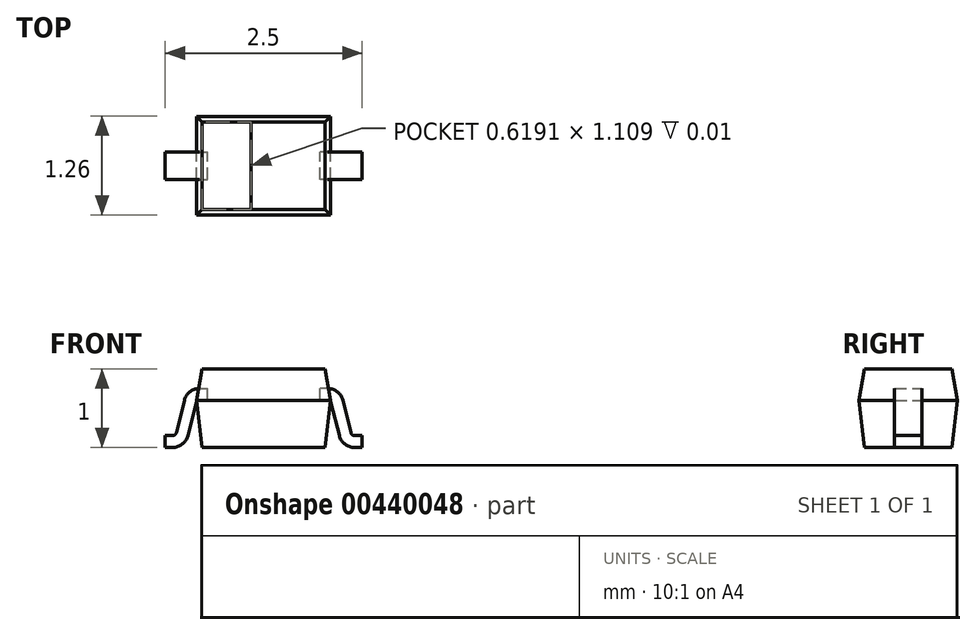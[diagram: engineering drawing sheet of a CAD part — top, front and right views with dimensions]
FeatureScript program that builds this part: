
annotation { "Feature Type Name" : "Feature", "Feature Type Description" : "" }
export const myFeature = defineFeature(function(context is Context, id is Id, definition is map)
    precondition{}
    {
        {
            var Q0;
            Q0=qCreatedBy(makeId("Front.planeOp"),FACE);
            var sketch = newSketch(context, id + "F0", { "sketchPlane" : qUnion([Q0])});
            skLineSegment(sketch, "E0", {"start": v(-0.85, 0) * mm, "end": v(0.85, 0) * mm});
            skLineSegment(sketch, "E1", {"start": v(0.85, 0) * mm, "end": v(0.78, 0.4) * mm});
            skLineSegment(sketch, "E2", {"start": v(0.78, 0.4) * mm, "end": v(-0.78, 0.4) * mm});
            skLineSegment(sketch, "E3", {"start": v(-0.78, 0.4) * mm, "end": v(-0.85, 0) * mm});
            skLineSegment(sketch, "E4", {"start": v(-0.85, 0) * mm, "end": v(-0.78, -0.6) * mm});
            skLineSegment(sketch, "E5", {"start": v(-0.78, -0.6) * mm, "end": v(0.78, -0.6) * mm});
            skLineSegment(sketch, "E6", {"start": v(0.78, -0.6) * mm, "end": v(0.85, 0) * mm});
            skLineSegment(sketch, "E7", {"start": v(0, 0.4) * mm, "end": v(0, -0.6) * mm});
            skSolve(sketch);
        }
        {
            var Q0;
            Q0 = qSketchRegion(id + "F0", true);
            extrude(context, id + "F1", {"entities" : qUnion([Q0]), "endBound" : BoundingType.SYMMETRIC, "depth" : 1.25 * mm});
        }
        {
            var Q0;
            Q0=qCreatedBy(makeId("Right.planeOp"),FACE);
            var sketch = newSketch(context, id + "F2", { "sketchPlane" : qUnion([Q0])});
            skLineSegment(sketch, "E8.0.0", {"start": v(0.62, -0.6) * mm, "end": v(0.62, 0) * mm});
            skLineSegment(sketch, "E8.0.1", {"start": v(0.62, 0) * mm, "end": v(-0.62, 0) * mm});
            skLineSegment(sketch, "E8.0.2", {"start": v(-0.62, 0) * mm, "end": v(-0.62, -0.6) * mm});
            skLineSegment(sketch, "E9.0.0", {"start": v(0.62, 0) * mm, "end": v(0.62, 0.4) * mm});
            skLineSegment(sketch, "E9.0.1", {"start": v(0.62, 0.4) * mm, "end": v(-0.62, 0.4) * mm});
            skLineSegment(sketch, "E9.0.2", {"start": v(-0.62, 0.4) * mm, "end": v(-0.62, 0) * mm});
            skLineSegment(sketch, "E9.0.3", {"start": v(-0.62, 0) * mm, "end": v(0.62, 0) * mm});
            skLineSegment(sketch, "E10", {"start": v(-0.63, 0) * mm, "end": v(-0.55, 0.4) * mm});
            skLineSegment(sketch, "E11", {"start": v(0.62, 0) * mm, "end": v(0.55, 0.4) * mm});
            skLineSegment(sketch, "E12", {"start": v(0.55, 0.4) * mm, "end": v(-0.55, 0.4) * mm});
            skLineSegment(sketch, "E13", {"start": v(-0.62, 0) * mm, "end": v(-0.55, -0.6) * mm});
            skLineSegment(sketch, "E14", {"start": v(0.62, 0) * mm, "end": v(0.55, -0.6) * mm});
            skLineSegment(sketch, "E15", {"start": v(0.55, -0.6) * mm, "end": v(-0.55, -0.6) * mm});
            skLineSegment(sketch, "E16", {"start": v(0, -0.6) * mm, "end": v(0, 0.4) * mm});
            skLineSegment(sketch, "E17.0", {"start": v(-0.62, -0.6) * mm, "end": v(0.62, -0.6) * mm});
            skLineSegment(sketch, "E18", {"start": v(-0.62, -0.6) * mm, "end": v(-0.55, -0.6) * mm});
            skSolve(sketch);
        }
        {
            var Q0;
            {var subQ0=sQuery(id+"F2.wireOp",EDGE,"E9.0.2");Q0=makeQuery(id+"F2.imprint","IMPRINT",FACE,{"disambiguationData":[TD([[makeQuery(id+"F2.imprint","IMPRINT",EDGE,{"derivedFrom":subQ0}),1.0]])]});}
            var Q1;
            Q1=makeQuery(id+"F2.imprint","IMPRINT",FACE,{"disambiguationData":[TD([[makeQuery(id+"F2.imprint","IMPRINT",EDGE,{"derivedFrom":sQuery(id+"F2.wireOp",EDGE,"E13")}),-1.0]])]});
            var Q2;
            {var subQ0=sQuery(id+"F2.wireOp",EDGE,"E8.0.0");Q2=makeQuery(id+"F2.imprint","IMPRINT",FACE,{"disambiguationData":[TD([[makeQuery(id+"F2.imprint","IMPRINT",EDGE,{"derivedFrom":subQ0}),1.0]])]});}
            var Q3;
            {var subQ0=sQuery(id+"F2.wireOp",EDGE,"E9.0.0");Q3=makeQuery(id+"F2.imprint","IMPRINT",FACE,{"disambiguationData":[TD([[makeQuery(id+"F2.imprint","IMPRINT",EDGE,{"derivedFrom":subQ0}),1.0]])]});}
            extrude(context, id + "F3", {"entities" : qUnion([Q0, Q1, Q2, Q3]), "operationType" : NewBodyOperationType.REMOVE, "endBound" : BoundingType.THROUGH_ALL, "oppositeDirection" : true, "depth" : 25 * mm, "hasSecondDirection" : true, "secondDirectionBound" : SecondDirectionBoundingType.THROUGH_ALL, "secondDirectionOppositeDirection" : false, "secondDirectionDepth" : 25 * mm});
        }
        {
            var Q0;
            Q0=qCreatedBy(makeId("Front.planeOp"),FACE);
            var sketch = newSketch(context, id + "F4", { "sketchPlane" : qUnion([Q0])});
            skLineSegment(sketch, "E19.0", {"start": v(-0.78, 0.4) * mm, "end": v(0.78, 0.4) * mm});
            skLineSegment(sketch, "E20.0", {"start": v(-0.78, -0.6) * mm, "end": v(0.78, -0.6) * mm});
            skLineSegment(sketch, "E21", {"start": v(0, 0.4) * mm, "end": v(0, -0.6) * mm});
            skLineSegment(sketch, "E22", {"start": v(1.25, -0.6) * mm, "end": v(-1.25, -0.6) * mm, "construction": true});
            skPoint(sketch, "E23.0", {"position": v(0.85, 0) * mm});
            skLineSegment(sketch, "E24", {"start": v(1.25, -0.6) * mm, "end": v(1.16, -0.6) * mm});
            skLineSegment(sketch, "E25", {"start": v(0.96, -0.45) * mm, "end": v(0.86, -0.04) * mm});
            skLineSegment(sketch, "E26", {"start": v(-1.25, -0.6) * mm, "end": v(-1.16, -0.6) * mm});
            skPoint(sketch, "E27.visualSharp", {"position": v(1, -0.6) * mm});
            skArc(sketch, "E27.filletArc", {"start": v(0.96, -0.45) * mm, "mid": v(1.03, -0.56) * mm, "end": v(1.16, -0.6) * mm});
            skLineSegment(sketch, "E28", {"start": v(0.81, 0) * mm, "end": v(0.71, 0) * mm});
            skArc(sketch, "E29.filletArc", {"start": v(0.86, -0.04) * mm, "mid": v(0.84, -0.01) * mm, "end": v(0.81, 0) * mm});
            skLineSegment(sketch, "E30.0", {"start": v(0.81, 0.15) * mm, "end": v(0.71, 0.15) * mm});
            skLineSegment(sketch, "E30.1", {"start": v(1.25, -0.45) * mm, "end": v(1.16, -0.45) * mm});
            skArc(sketch, "E30.2", {"start": v(1.1, -0.41) * mm, "mid": v(1.13, -0.44) * mm, "end": v(1.16, -0.45) * mm});
            skLineSegment(sketch, "E30.3", {"start": v(1.1, -0.41) * mm, "end": v(1, 0) * mm});
            skArc(sketch, "E30.4", {"start": v(1, 0) * mm, "mid": v(0.93, 0.1) * mm, "end": v(0.81, 0.15) * mm});
            skLineSegment(sketch, "E31", {"start": v(1.25, -0.6) * mm, "end": v(1.25, -0.45) * mm});
            skLineSegment(sketch, "E32", {"start": v(0.71, 0) * mm, "end": v(0.71, 0.15) * mm});
            skArc(sketch, "E33.MirrorCS", {"start": v(-0.86, -0.04) * mm, "mid": v(-0.84, -0.01) * mm, "end": v(-0.81, 0) * mm});
            skPoint(sketch, "E34.MirrorP", {"position": v(-0.85, 0) * mm});
            skLineSegment(sketch, "E35.MirrorCS", {"start": v(0.78, -0.6) * mm, "end": v(-0.78, -0.6) * mm});
            skArc(sketch, "E36.MirrorCS", {"start": v(-1.1, -0.41) * mm, "mid": v(-1.13, -0.44) * mm, "end": v(-1.16, -0.45) * mm});
            skLineSegment(sketch, "E37.MirrorCS", {"start": v(-0.81, 0.15) * mm, "end": v(-0.71, 0.15) * mm});
            skArc(sketch, "E38.MirrorCS", {"start": v(-0.96, -0.45) * mm, "mid": v(-1.03, -0.56) * mm, "end": v(-1.16, -0.6) * mm});
            skLineSegment(sketch, "E39.MirrorCS", {"start": v(-1.25, -0.45) * mm, "end": v(-1.16, -0.45) * mm});
            skArc(sketch, "E40.MirrorCS", {"start": v(-1, 0) * mm, "mid": v(-0.93, 0.1) * mm, "end": v(-0.81, 0.15) * mm});
            skLineSegment(sketch, "E41.MirrorCS", {"start": v(-1.25, -0.6) * mm, "end": v(-1.25, -0.45) * mm});
            skLineSegment(sketch, "E42.MirrorCS", {"start": v(-1.1, -0.41) * mm, "end": v(-1, 0) * mm});
            skPoint(sketch, "E43.MirrorP", {"position": v(-1, -0.6) * mm});
            skLineSegment(sketch, "E44.MirrorCS", {"start": v(-0.71, 0) * mm, "end": v(-0.71, 0.15) * mm});
            skLineSegment(sketch, "E45.MirrorCS", {"start": v(-1.25, -0.6) * mm, "end": v(1.25, -0.6) * mm, "construction": true});
            skLineSegment(sketch, "E46.MirrorCS", {"start": v(-0.81, 0) * mm, "end": v(-0.71, 0) * mm});
            skLineSegment(sketch, "E47.MirrorCS", {"start": v(-0.96, -0.45) * mm, "end": v(-0.86, -0.04) * mm});
            skSolve(sketch);
        }
        {
            var Q0;
            Q0 = qSketchRegion(id + "F4", true);
            extrude(context, id + "F5", {"entities" : qUnion([Q0]), "endBound" : BoundingType.SYMMETRIC, "depth" : 0.35 * mm});
        }
        {
            var Q0;
            Q0=makeQuery(id+"F1.opExtrude","SWEPT_FACE",FACE,{"disambiguationData":[OSD([sQuery(id+"F0.wireOp",EDGE,"E2")])]});
            var sketch = newSketch(context, id + "F6", { "sketchPlane" : qUnion([Q0])});
            skLineSegment(sketch, "E48.bottom", {"start": v(-0.78, 0.55) * mm, "end": v(-0.16, 0.55) * mm});
            skLineSegment(sketch, "E48.top", {"start": v(-0.78, -0.55) * mm, "end": v(-0.16, -0.55) * mm});
            skLineSegment(sketch, "E48.left", {"start": v(-0.78, 0.55) * mm, "end": v(-0.78, -0.55) * mm});
            skLineSegment(sketch, "E48.right", {"start": v(-0.16, 0.55) * mm, "end": v(-0.16, -0.55) * mm});
            skSolve(sketch);
        }
        {
            var Q0;
            Q0 = qSketchRegion(id + "F6", true);
            var Q1;
            Q1=sQuery(id+"F6.wireOp",EDGE,"E48.right");
            var Q2;
            Q2=sQuery(id+"F6.wireOp",EDGE,"E48.bottom");
            var Q3;
            Q3=sQuery(id+"F6.wireOp",EDGE,"E48.left");
            var Q4;
            Q4=sQuery(id+"F6.wireOp",EDGE,"E48.top");
            extrude(context, id + "F7", {"entities" : qUnion([Q0]), "operationType" : NewBodyOperationType.REMOVE, "surfaceEntities" : qUnion([Q1, Q2, Q3, Q4]), "oppositeDirection" : true, "depth" : 0.01 * mm});
        }
    });
